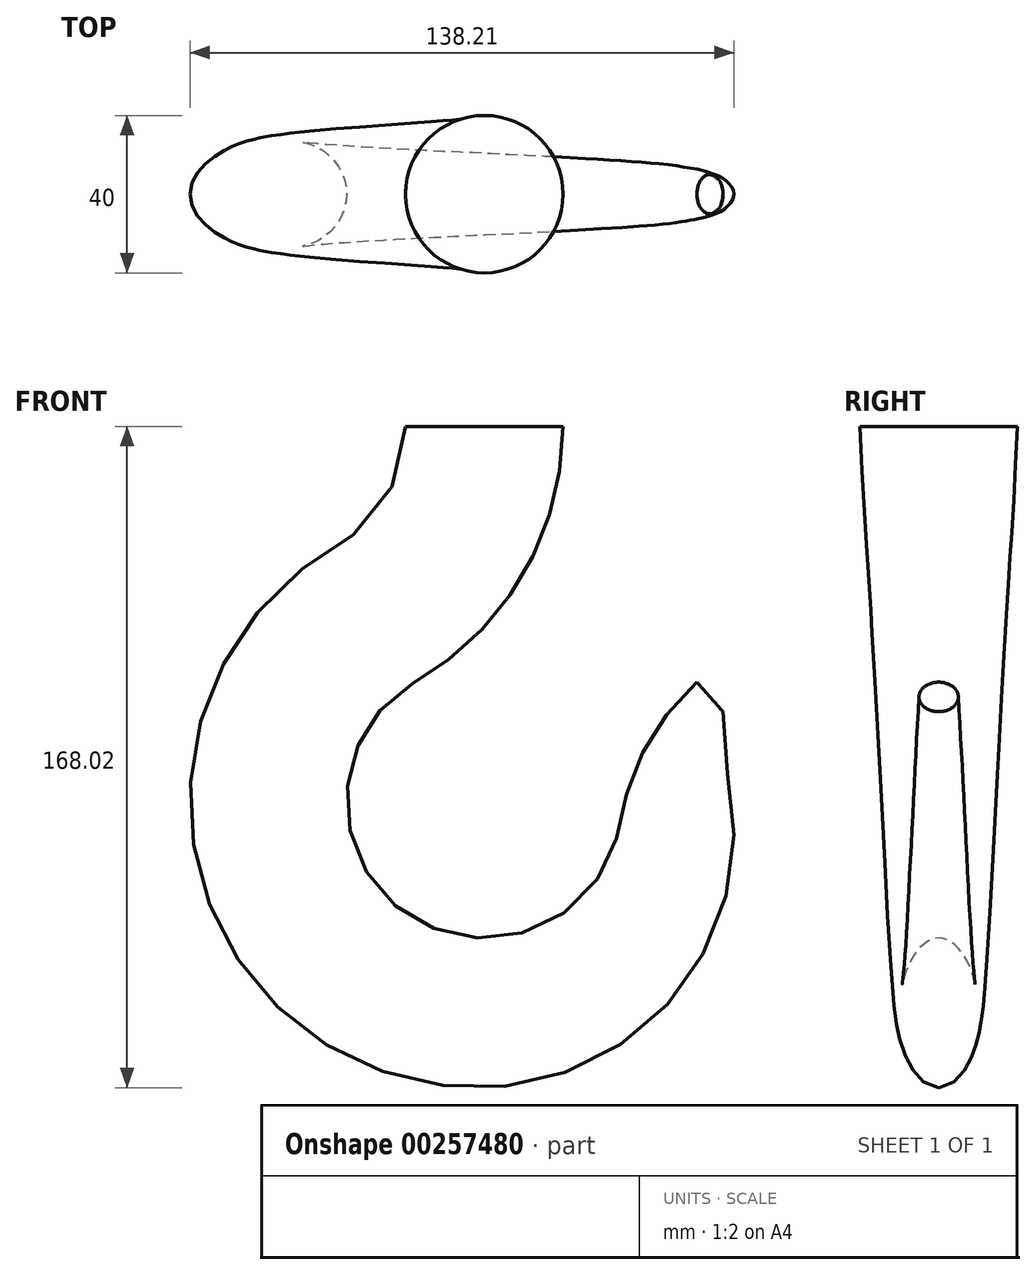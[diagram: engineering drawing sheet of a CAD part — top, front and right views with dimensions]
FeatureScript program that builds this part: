
annotation { "Feature Type Name" : "Feature", "Feature Type Description" : "" }
export const myFeature = defineFeature(function(context is Context, id is Id, definition is map)
    precondition{}
    {
        {
            var Q0;
            Q0=qCreatedBy(makeId("Front.planeOp"),FACE);
            var sketch = newSketch(context, id + "F0", { "sketchPlane" : qUnion([Q0])});
            skLineSegment(sketch, "E0", {"start": v(0, 17.35) * mm, "end": v(0, -189.4) * mm, "construction": true});
            skLineSegment(sketch, "E1", {"start": v(-120.84, -95) * mm, "end": v(144.63, -95) * mm, "construction": true});
            skLineSegment(sketch, "E2", {"start": v(20, 0) * mm, "end": v(-20, 0) * mm});
            skArc(sketch, "E3", {"start": v(-20, 0) * mm, "mid": v(-24.68, -17.48) * mm, "end": v(-37.46, -30.29) * mm});
            skArc(sketch, "E4", {"start": v(20, 0) * mm, "mid": v(9.9, -37.58) * mm, "end": v(-17.66, -65.04) * mm});
            skPoint(sketch, "E5", {"position": v(0, -168) * mm});
            skPoint(sketch, "E6", {"position": v(0, -95) * mm});
            skArc(sketch, "E7", {"start": v(-37.46, -30.29) * mm, "mid": v(-64.78, -57.65) * mm, "end": v(-74.77, -95) * mm});
            skArc(sketch, "E8", {"start": v(-35, -95) * mm, "mid": v(-24.75, -119.75) * mm, "end": v(0, -130) * mm});
            skArc(sketch, "E9", {"start": v(-74.77, -95) * mm, "mid": v(-52.76, -147.25) * mm, "end": v(0, -168) * mm});
            skArc(sketch, "E10", {"start": v(-35, -95) * mm, "mid": v(-30.35, -77.7) * mm, "end": v(-17.66, -65.04) * mm});
            skArc(sketch, "E11", {"start": v(0, -168) * mm, "mid": v(49.83, -142.83) * mm, "end": v(61.75, -88.29) * mm});
            skArc(sketch, "E12", {"start": v(60.65, -72.48) * mm, "mid": v(60.57, -80.43) * mm, "end": v(61.75, -88.29) * mm});
            skLineSegment(sketch, "E13", {"start": v(60.65, -72.48) * mm, "end": v(54.02, -65) * mm});
            skArc(sketch, "E14", {"start": v(54.02, -65) * mm, "mid": v(41.2, -81.05) * mm, "end": v(34.57, -100.49) * mm});
            skArc(sketch, "E15", {"start": v(0, -130) * mm, "mid": v(22.73, -121.62) * mm, "end": v(34.57, -100.49) * mm});
            skCircle(sketch, "E16", {"center": v(57.33, -68.74) * mm, "radius": 5 * mm, "construction": true});
            skSolve(sketch);
        }
        {
            var Q0;
            Q0=qCreatedBy(makeId("Top.planeOp"),FACE);
            var sketch = newSketch(context, id + "F1", { "sketchPlane" : qUnion([Q0])});
            skPoint(sketch, "E17.0", {"position": v(-20, 0) * mm});
            skPoint(sketch, "E18.0", {"position": v(0, 0) * mm});
            skPoint(sketch, "E19.0", {"position": v(20, 0) * mm});
            skCircle(sketch, "E20", {"center": v(0, 0) * mm, "radius": 20 * mm});
            skSolve(sketch);
        }
        {
            var Q0;
            Q0=sQuery(id+"F0.wireOp",EDGE,"E13");
            cPlane(context, id + "F2", {"entities" : qUnion([Q0]), "cplaneType" : CPlaneType.LINE_ANGLE, "offset" : 25 * mm, "angle" : 0 * degree, "width" : 150 * mm, "height" : 150 * mm});
        }
        {
            var Q0;
            Q0=qCreatedBy(id+"F2.planeOp",FACE);
            var sketch = newSketch(context, id + "F3", { "sketchPlane" : qUnion([Q0])});
            skPoint(sketch, "E21.0", {"position": v(0, -89.47) * mm});
            skPoint(sketch, "E22.0", {"position": v(0, -84.47) * mm});
            skPoint(sketch, "E23.0", {"position": v(0, -94.47) * mm});
            skCircle(sketch, "E24", {"center": v(0, -89.47) * mm, "radius": 5 * mm});
            skSolve(sketch);
        }
        {
            var Q0;
            Q0=qCreatedBy(makeId("Front.planeOp"),FACE);
            var sketch = newSketch(context, id + "F4", { "sketchPlane" : qUnion([Q0])});
            skArc(sketch, "E25.0", {"start": v(-20, 0) * mm, "mid": v(-24.68, -17.48) * mm, "end": v(-37.46, -30.29) * mm});
            skArc(sketch, "E26.0", {"start": v(-37.46, -30.29) * mm, "mid": v(-64.78, -57.65) * mm, "end": v(-74.77, -95) * mm});
            skArc(sketch, "E27.0", {"start": v(-74.77, -95) * mm, "mid": v(-52.76, -147.25) * mm, "end": v(0, -168) * mm});
            skArc(sketch, "E28.0", {"start": v(0, -168) * mm, "mid": v(49.83, -142.83) * mm, "end": v(61.75, -88.29) * mm});
            skArc(sketch, "E29.0", {"start": v(60.65, -72.48) * mm, "mid": v(60.57, -80.43) * mm, "end": v(61.75, -88.29) * mm});
            skSolve(sketch);
        }
        {
            var Q0;
            Q0=qCreatedBy(makeId("Front.planeOp"),FACE);
            var sketch = newSketch(context, id + "F5", { "sketchPlane" : qUnion([Q0])});
            skArc(sketch, "E30.0", {"start": v(20, 0) * mm, "mid": v(9.9, -37.58) * mm, "end": v(-17.66, -65.04) * mm});
            skArc(sketch, "E31.0", {"start": v(-35, -95) * mm, "mid": v(-30.35, -77.7) * mm, "end": v(-17.66, -65.04) * mm});
            skArc(sketch, "E32.0", {"start": v(-35, -95) * mm, "mid": v(-24.75, -119.75) * mm, "end": v(0, -130) * mm});
            skArc(sketch, "E33.0", {"start": v(0, -130) * mm, "mid": v(22.73, -121.62) * mm, "end": v(34.57, -100.49) * mm});
            skArc(sketch, "E34.0", {"start": v(54.02, -65) * mm, "mid": v(41.2, -81.05) * mm, "end": v(34.57, -100.49) * mm});
            skSolve(sketch);
        }
        {
            var Q0;
            Q0=makeQuery(id+"F1.imprint","IMPRINT",FACE,{"disambiguationData":[TD([[makeQuery(id+"F1.imprint","IMPRINT",EDGE,{"derivedFrom":sQuery(id+"F1.wireOp",EDGE,"E20")}),1.0]])]});
            var Q1;
            Q1=makeQuery(id+"F3.imprint","IMPRINT",FACE,{"disambiguationData":[TD([[makeQuery(id+"F3.imprint","IMPRINT",EDGE,{"derivedFrom":sQuery(id+"F3.wireOp",EDGE,"E24")}),1.0]])]});
            var Q2;
            Q2 = qConstructionFilter(qBodyType(qCreatedBy(id + "F4" ,EDGE), BodyType.WIRE), ConstructionObject.NO);
            var Q3;
            Q3 = qConstructionFilter(qBodyType(qCreatedBy(id + "F5" ,EDGE), BodyType.WIRE), ConstructionObject.NO);
            loft(context, id + "F6", {"addGuides" : true, "sheetProfilesArray" : [{ "sheetProfileEntities" : qUnion([Q0]) }, { "sheetProfileEntities" : qUnion([Q1]) }], "guidesArray" : [{ "guideEntities" : qUnion([Q2]), "guideDerivativeType" : LoftGuideDerivativeType.DEFAULT, "guideDerivativeMagnitude" : 1 }, { "guideEntities" : qUnion([Q3]), "guideDerivativeType" : LoftGuideDerivativeType.DEFAULT, "guideDerivativeMagnitude" : 1 }]});
        }
    });
